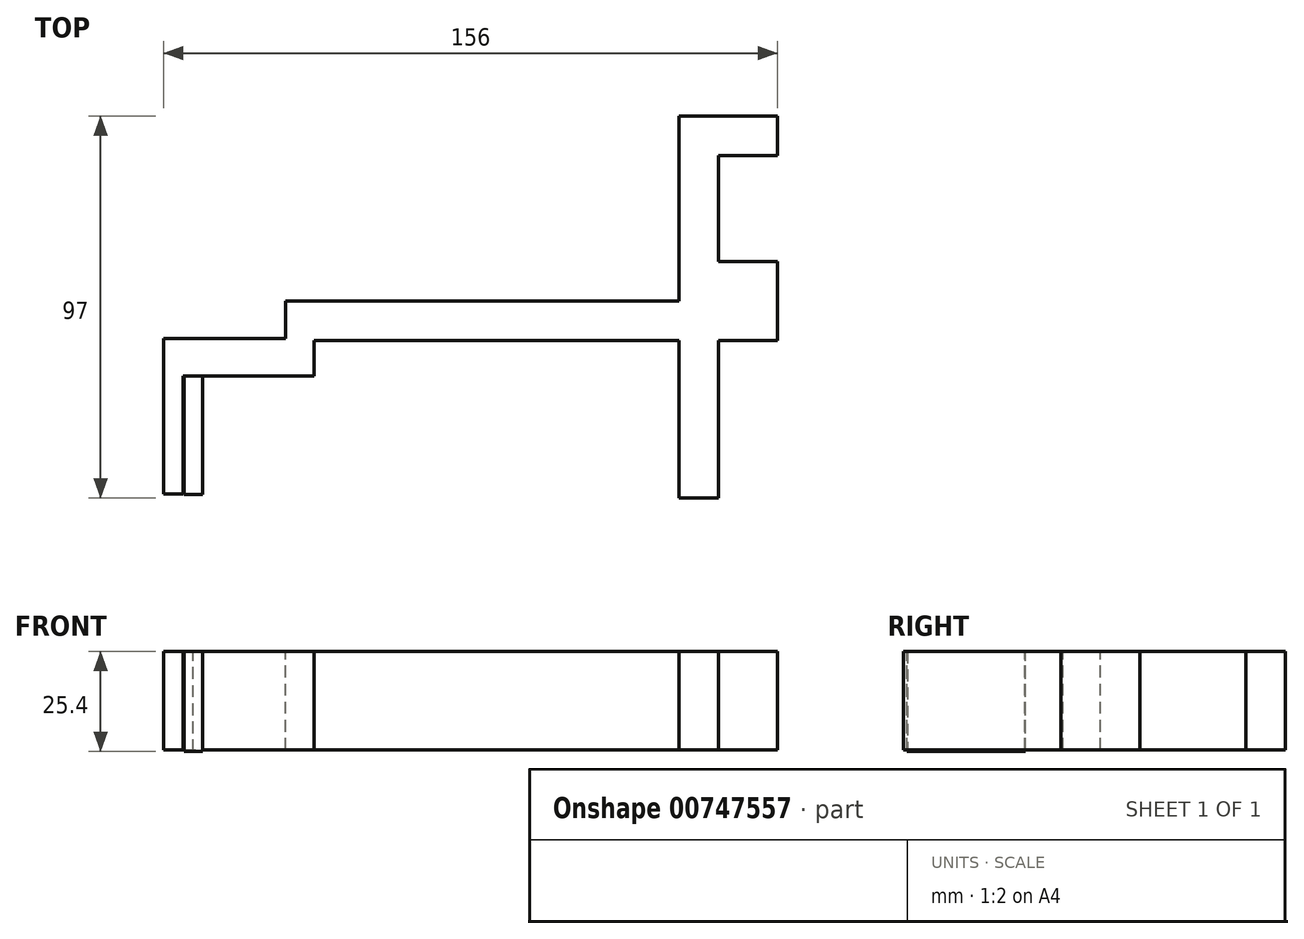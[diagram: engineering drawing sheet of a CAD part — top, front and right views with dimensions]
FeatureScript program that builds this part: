
annotation { "Feature Type Name" : "Feature", "Feature Type Description" : "" }
export const myFeature = defineFeature(function(context is Context, id is Id, definition is map)
    precondition{}
    {
        {
            var Q0;
            Q0=qCreatedBy(makeId("Front.planeOp"),FACE);
            var sketch = newSketch(context, id + "F0", { "sketchPlane" : qUnion([Q0])});
            skLineSegment(sketch, "E0.bottom", {"start": v(-55.45, 37.09) * mm, "end": v(59.55, 37.09) * mm});
            skLineSegment(sketch, "E0.top", {"start": v(-55.45, 12.09) * mm, "end": v(59.55, 12.09) * mm});
            skLineSegment(sketch, "E0.left", {"start": v(-55.45, 37.09) * mm, "end": v(-55.45, 12.09) * mm});
            skLineSegment(sketch, "E0.right", {"start": v(59.55, 37.09) * mm, "end": v(59.55, 12.09) * mm});
            skSolve(sketch);
        }
        {
            var Q0;
            Q0=makeQuery(id+"F0.imprint","IMPRINT",FACE,{"disambiguationData":[TD([[makeQuery(id+"F0.imprint","IMPRINT",EDGE,{"derivedFrom":sQuery(id+"F0.wireOp",EDGE,"E0.bottom")}),-1.0]])]});
            extrude(context, id + "F1", {"entities" : qUnion([Q0]), "depth" : 10 * mm, "offsetDistance" : 25.4 * mm});
        }
        {
            var Q0;
            Q0=makeQuery(id+"F1.opExtrude","CAP_FACE",FACE,{"disambiguationData":[OSD([sQuery(id+"F0.wireOp",EDGE,"E0.bottom"),sQuery(id+"F0.wireOp",EDGE,"E0.top"),sQuery(id+"F0.wireOp",EDGE,"E0.left"),sQuery(id+"F0.wireOp",EDGE,"E0.right")])],"isStart":false});
            var sketch = newSketch(context, id + "F2", { "sketchPlane" : qUnion([Q0])});
            skLineSegment(sketch, "E1", {"start": v(-55.45, 37.09) * mm, "end": v(-45.45, 37.09) * mm});
            skLineSegment(sketch, "E2", {"start": v(-45.45, 37.09) * mm, "end": v(-45.45, 12.09) * mm});
            skLineSegment(sketch, "E3", {"start": v(-45.45, 12.09) * mm, "end": v(-55.45, 12.09) * mm});
            skLineSegment(sketch, "E4", {"start": v(-55.45, 12.09) * mm, "end": v(-55.45, 37.09) * mm});
            skSolve(sketch);
        }
        {
            var Q0;
            Q0=makeQuery(id+"F2.imprint","IMPRINT",FACE,{"disambiguationData":[TD([[makeQuery(id+"F2.imprint","IMPRINT",EDGE,{"derivedFrom":sQuery(id+"F2.wireOp",EDGE,"E1")}),-1.0]])]});
            extrude(context, id + "F3", {"entities" : qUnion([Q0]), "operationType" : NewBodyOperationType.ADD, "depth" : 9.05 * mm, "offsetDistance" : 25.4 * mm});
        }
        {
            var Q0;
            Q0=makeQuery(id+"F1.opExtrude","CAP_FACE",FACE,{"disambiguationData":[OSD([sQuery(id+"F0.wireOp",EDGE,"E0.bottom"),sQuery(id+"F0.wireOp",EDGE,"E0.top"),sQuery(id+"F0.wireOp",EDGE,"E0.left"),sQuery(id+"F0.wireOp",EDGE,"E0.right")])],"isStart":false});
            var sketch = newSketch(context, id + "F4", { "sketchPlane" : qUnion([Q0])});
            skLineSegment(sketch, "E5", {"start": v(59.55, 8.34) * mm, "end": v(54.55, 8.34) * mm});
            skLineSegment(sketch, "E6", {"start": v(54.55, 12.09) * mm, "end": v(44.55, 12.09) * mm});
            skLineSegment(sketch, "E7", {"start": v(54.55, 12.09) * mm, "end": v(54.55, 37.09) * mm});
            skLineSegment(sketch, "E8", {"start": v(44.55, 12.09) * mm, "end": v(44.55, 37.09) * mm});
            skLineSegment(sketch, "E9", {"start": v(44.55, 37.09) * mm, "end": v(54.55, 37.09) * mm});
            skSolve(sketch);
        }
        {
            var Q0;
            Q0=makeQuery(id+"F4.imprint","IMPRINT",FACE,{"disambiguationData":[TD([[makeQuery(id+"F4.imprint","IMPRINT",EDGE,{"derivedFrom":sQuery(id+"F4.wireOp",EDGE,"E6")}),1.0]])]});
            extrude(context, id + "F5", {"entities" : qUnion([Q0]), "operationType" : NewBodyOperationType.ADD, "depth" : 40 * mm, "offsetDistance" : 25.4 * mm});
        }
        {
            var Q0;
            Q0=makeQuery(id+"F1.opExtrude","CAP_FACE",FACE,{"disambiguationData":[OSD([sQuery(id+"F0.wireOp",EDGE,"E0.bottom"),sQuery(id+"F0.wireOp",EDGE,"E0.top"),sQuery(id+"F0.wireOp",EDGE,"E0.left"),sQuery(id+"F0.wireOp",EDGE,"E0.right")])],"isStart":true});
            var sketch = newSketch(context, id + "F6", { "sketchPlane" : qUnion([Q0])});
            skLineSegment(sketch, "E10", {"start": v(-59.55, -12.94) * mm, "end": v(-44.55, -12.94) * mm});
            skLineSegment(sketch, "E11", {"start": v(-59.55, 12.09) * mm, "end": v(-44.55, 12.09) * mm});
            skLineSegment(sketch, "E12", {"start": v(-44.55, 12.09) * mm, "end": v(-44.55, 37.09) * mm});
            skLineSegment(sketch, "E13", {"start": v(-44.55, 37.09) * mm, "end": v(-59.55, 37.09) * mm});
            skLineSegment(sketch, "E14", {"start": v(-59.55, 37.09) * mm, "end": v(-59.55, 12.09) * mm});
            skSolve(sketch);
        }
        {
            var Q0;
            Q0=makeQuery(id+"F6.imprint","IMPRINT",FACE,{"disambiguationData":[TD([[makeQuery(id+"F6.imprint","IMPRINT",EDGE,{"derivedFrom":sQuery(id+"F6.wireOp",EDGE,"E11")}),-1.0]])]});
            extrude(context, id + "F7", {"entities" : qUnion([Q0]), "operationType" : NewBodyOperationType.ADD, "depth" : 47 * mm, "offsetDistance" : 25.4 * mm});
        }
        {
            var Q0;
            Q0=makeQuery(id+"F7.boolean.opBoolean","MERGE",FACE,{"derivedFrom":[makeQuery(id+"F5.boolean.opBoolean","MERGE",FACE,{"derivedFrom":[makeQuery(id+"F3.boolean.opBoolean","MERGE",FACE,{"derivedFrom":[makeQuery(id+"F1.opExtrude","SWEPT_FACE",FACE,{"disambiguationData":[OSD([sQuery(id+"F0.wireOp",EDGE,"E0.top")])]}),makeQuery(id+"F3.opExtrude","SWEPT_FACE",FACE,{"disambiguationData":[OSD([sQuery(id+"F2.wireOp",EDGE,"E3")])]})]}),makeQuery(id+"F5.opExtrude","SWEPT_FACE",FACE,{"disambiguationData":[OSD([sQuery(id+"F4.wireOp",EDGE,"E6")])]})]}),makeQuery(id+"F7.opExtrude","SWEPT_FACE",FACE,{"disambiguationData":[OSD([sQuery(id+"F6.wireOp",EDGE,"E11")])]})]});
            var sketch = newSketch(context, id + "F8", { "sketchPlane" : qUnion([Q0])});
            skLineSegment(sketch, "E15", {"start": v(51.76, 0) * mm, "end": v(51.76, -10) * mm});
            skLineSegment(sketch, "E16", {"start": v(59.55, -68.62) * mm, "end": v(54.55, -68.62) * mm});
            skLineSegment(sketch, "E17", {"start": v(59.55, -10) * mm, "end": v(59.55, -37) * mm});
            skLineSegment(sketch, "E18", {"start": v(54.55, -10) * mm, "end": v(59.55, -10) * mm});
            skLineSegment(sketch, "E19", {"start": v(54.55, -37) * mm, "end": v(59.55, -37) * mm});
            skLineSegment(sketch, "E20", {"start": v(54.55, -10) * mm, "end": v(54.55, -37) * mm});
            skSolve(sketch);
        }
        {
            var Q0;
            Q0=makeQuery(id+"F8.imprint","IMPRINT",FACE,{"disambiguationData":[TD([[makeQuery(id+"F8.imprint","IMPRINT",EDGE,{"derivedFrom":sQuery(id+"F8.wireOp",EDGE,"E17")}),-1.0]])]});
            extrude(context, id + "F9", {"entities" : qUnion([Q0]), "operationType" : NewBodyOperationType.REMOVE, "oppositeDirection" : true, "depth" : 25 * mm, "offsetDistance" : 25.4 * mm});
        }
        {
            var Q0;
            Q0=makeQuery(id+"F3.boolean.opBoolean","MERGE",FACE,{"derivedFrom":[makeQuery(id+"F1.opExtrude","SWEPT_FACE",FACE,{"disambiguationData":[OSD([sQuery(id+"F0.wireOp",EDGE,"E0.left")])]}),makeQuery(id+"F3.opExtrude","SWEPT_FACE",FACE,{"disambiguationData":[OSD([sQuery(id+"F2.wireOp",EDGE,"E4")])]})]});
            var sketch = newSketch(context, id + "F10", { "sketchPlane" : qUnion([Q0])});
            skLineSegment(sketch, "E21", {"start": v(19.05, 12.09) * mm, "end": v(9.53, 12.09) * mm});
            skLineSegment(sketch, "E22", {"start": v(9.53, 12.09) * mm, "end": v(9.53, 37.09) * mm});
            skLineSegment(sketch, "E23", {"start": v(9.53, 37.09) * mm, "end": v(19.05, 37.09) * mm});
            skSolve(sketch);
        }
        {
            var Q0;
            Q0=makeQuery(id+"F10.imprint","IMPRINT",FACE,{"disambiguationData":[TD([[makeQuery(id+"F10.imprint","IMPRINT",EDGE,{"derivedFrom":sQuery(id+"F10.wireOp",EDGE,"E21")}),-1.0]])]});
            extrude(context, id + "F11", {"entities" : qUnion([Q0]), "operationType" : NewBodyOperationType.ADD, "depth" : 36 * mm, "offsetDistance" : 25.4 * mm});
        }
        {
            var Q0;
            {var subQ0=sQuery(id+"F2.wireOp",EDGE,"E4");Q0=makeQuery(id+"F11.boolean.opBoolean","MERGE",FACE,{"derivedFrom":[makeQuery(id+"F3.opExtrude","CAP_FACE",FACE,{"disambiguationData":[OSD([sQuery(id+"F2.wireOp",EDGE,"E1"),sQuery(id+"F2.wireOp",EDGE,"E2"),sQuery(id+"F2.wireOp",EDGE,"E3"),subQ0])],"isStart":false}),makeQuery(id+"F11.opExtrude","SWEPT_FACE",FACE,{"disambiguationData":[OSD([subQ0])]})]});}
            var sketch = newSketch(context, id + "F12", { "sketchPlane" : qUnion([Q0])});
            skLineSegment(sketch, "E24", {"start": v(-91.45, 37.09) * mm, "end": v(-81.45, 37.09) * mm});
            skLineSegment(sketch, "E25", {"start": v(-81.45, 37.09) * mm, "end": v(-81.45, 12.09) * mm});
            skLineSegment(sketch, "E26", {"start": v(-81.45, 12.09) * mm, "end": v(-91.45, 12.09) * mm});
            skLineSegment(sketch, "E27", {"start": v(-91.45, 12.09) * mm, "end": v(-91.45, 37.09) * mm});
            skSolve(sketch);
        }
        {
            var Q0;
            Q0=makeQuery(id+"F12.imprint","IMPRINT",FACE,{"disambiguationData":[TD([[makeQuery(id+"F12.imprint","IMPRINT",EDGE,{"derivedFrom":sQuery(id+"F12.wireOp",EDGE,"E24")}),-1.0]])]});
            extrude(context, id + "F13", {"entities" : qUnion([Q0]), "operationType" : NewBodyOperationType.ADD, "depth" : 30 * mm, "offsetDistance" : 25.4 * mm});
        }
        {
            var Q0;
            {var subQ1=sQuery(id+"F0.wireOp",EDGE,"E0.right");Q0=makeQuery(id+"F9.boolean.opBoolean","SPLIT",FACE,{"disambiguationData":[TD([makeQuery(id+"F9.opExtrude","SWEPT_FACE",FACE,{"disambiguationData":[OSD([sQuery(id+"F8.wireOp",EDGE,"E18")])]})])],"derivedFrom":makeQuery(id+"F7.boolean.opBoolean","MERGE",FACE,{"derivedFrom":[makeQuery(id+"F1.opExtrude","SWEPT_FACE",FACE,{"disambiguationData":[OSD([subQ1])]}),makeQuery(id+"F7.opExtrude","SWEPT_FACE",FACE,{"disambiguationData":[OSD([sQuery(id+"F6.wireOp",EDGE,"E14")])]})]})});}
            extrude(context, id + "F14", {"entities" : qUnion([Q0]), "operationType" : NewBodyOperationType.ADD, "depth" : 10 * mm, "offsetDistance" : 25.4 * mm});
        }
        {
            var Q0;
            {var subQ1=sQuery(id+"F6.wireOp",EDGE,"E14");Q0=makeQuery(id+"F9.boolean.opBoolean","SPLIT",FACE,{"disambiguationData":[TD([makeQuery(id+"F9.opExtrude","SWEPT_FACE",FACE,{"disambiguationData":[OSD([sQuery(id+"F8.wireOp",EDGE,"E19")])]})])],"derivedFrom":makeQuery(id+"F7.boolean.opBoolean","MERGE",FACE,{"derivedFrom":[makeQuery(id+"F1.opExtrude","SWEPT_FACE",FACE,{"disambiguationData":[OSD([sQuery(id+"F0.wireOp",EDGE,"E0.right")])]}),makeQuery(id+"F7.opExtrude","SWEPT_FACE",FACE,{"disambiguationData":[OSD([subQ1])]})]})});}
            extrude(context, id + "F15", {"entities" : qUnion([Q0]), "operationType" : NewBodyOperationType.ADD, "depth" : 10 * mm, "offsetDistance" : 25.4 * mm});
        }
        {
            var Q0;
            {var subQ0=sQuery(id+"F6.wireOp",EDGE,"E14");var subQ1=sQuery(id+"F6.wireOp",EDGE,"E13");var subQ2=sQuery(id+"F0.wireOp",EDGE,"E0.right");var subQ3=sQuery(id+"F0.wireOp",EDGE,"E0.bottom");Q0=makeQuery(id+"F15.boolean.opBoolean","MERGE",FACE,{"derivedFrom":[makeQuery(id+"F14.boolean.opBoolean","MERGE",FACE,{"derivedFrom":[makeQuery(id+"F13.boolean.opBoolean","MERGE",FACE,{"derivedFrom":[makeQuery(id+"F11.boolean.opBoolean","MERGE",FACE,{"derivedFrom":[makeQuery(id+"F7.boolean.opBoolean","MERGE",FACE,{"derivedFrom":[makeQuery(id+"F5.boolean.opBoolean","MERGE",FACE,{"derivedFrom":[makeQuery(id+"F3.boolean.opBoolean","MERGE",FACE,{"derivedFrom":[makeQuery(id+"F1.opExtrude","SWEPT_FACE",FACE,{"disambiguationData":[OSD([subQ3])]}),makeQuery(id+"F3.opExtrude","SWEPT_FACE",FACE,{"disambiguationData":[OSD([sQuery(id+"F2.wireOp",EDGE,"E1")])]})]}),makeQuery(id+"F5.opExtrude","SWEPT_FACE",FACE,{"disambiguationData":[OSD([sQuery(id+"F4.wireOp",EDGE,"E9")])]})]}),makeQuery(id+"F7.opExtrude","SWEPT_FACE",FACE,{"disambiguationData":[OSD([subQ1])]})]}),makeQuery(id+"F11.opExtrude","SWEPT_FACE",FACE,{"disambiguationData":[OSD([sQuery(id+"F10.wireOp",EDGE,"E23")])]})]}),makeQuery(id+"F13.opExtrude","SWEPT_FACE",FACE,{"disambiguationData":[OSD([sQuery(id+"F12.wireOp",EDGE,"E24")])]})]}),makeQuery(id+"F14.opExtrude","SWEPT_FACE",FACE,{"disambiguationData":[OSD([subQ3,subQ2,subQ1,subQ0])]})]}),makeQuery(id+"F15.opExtrude","SWEPT_FACE",FACE,{"disambiguationData":[OSD([subQ3,subQ2,subQ1,subQ0])]})]});}
            var sketch = newSketch(context, id + "F16", { "sketchPlane" : qUnion([Q0])});
            skLineSegment(sketch, "E28", {"start": v(-45.45, -10) * mm, "end": v(-48.23, -10) * mm});
            skLineSegment(sketch, "E29", {"start": v(-48.23, -10) * mm, "end": v(-48.23, -19.05) * mm});
            skLineSegment(sketch, "E30", {"start": v(-48.23, -19.05) * mm, "end": v(-45.45, -19.05) * mm});
            skLineSegment(sketch, "E31", {"start": v(-45.45, -19.05) * mm, "end": v(-45.45, -10) * mm});
            skSolve(sketch);
        }
        {
            var Q0;
            Q0=makeQuery(id+"F16.imprint","IMPRINT",FACE,{"disambiguationData":[TD([[makeQuery(id+"F16.imprint","IMPRINT",EDGE,{"derivedFrom":sQuery(id+"F16.wireOp",EDGE,"E28")}),1.0]])]});
            extrude(context, id + "F17", {"entities" : qUnion([Q0]), "operationType" : NewBodyOperationType.REMOVE, "oppositeDirection" : true, "depth" : 25 * mm, "offsetDistance" : 25.4 * mm});
        }
        {
            var Q0;
            {var subQ0=sQuery(id+"F6.wireOp",EDGE,"E14");var subQ1=sQuery(id+"F6.wireOp",EDGE,"E13");var subQ2=sQuery(id+"F0.wireOp",EDGE,"E0.right");var subQ3=sQuery(id+"F0.wireOp",EDGE,"E0.bottom");Q0=makeQuery(id+"F15.boolean.opBoolean","MERGE",FACE,{"derivedFrom":[makeQuery(id+"F14.boolean.opBoolean","MERGE",FACE,{"derivedFrom":[makeQuery(id+"F13.boolean.opBoolean","MERGE",FACE,{"derivedFrom":[makeQuery(id+"F11.boolean.opBoolean","MERGE",FACE,{"derivedFrom":[makeQuery(id+"F7.boolean.opBoolean","MERGE",FACE,{"derivedFrom":[makeQuery(id+"F5.boolean.opBoolean","MERGE",FACE,{"derivedFrom":[makeQuery(id+"F3.boolean.opBoolean","MERGE",FACE,{"derivedFrom":[makeQuery(id+"F1.opExtrude","SWEPT_FACE",FACE,{"disambiguationData":[OSD([subQ3])]}),makeQuery(id+"F3.opExtrude","SWEPT_FACE",FACE,{"disambiguationData":[OSD([sQuery(id+"F2.wireOp",EDGE,"E1")])]})]}),makeQuery(id+"F5.opExtrude","SWEPT_FACE",FACE,{"disambiguationData":[OSD([sQuery(id+"F4.wireOp",EDGE,"E9")])]})]}),makeQuery(id+"F7.opExtrude","SWEPT_FACE",FACE,{"disambiguationData":[OSD([subQ1])]})]}),makeQuery(id+"F11.opExtrude","SWEPT_FACE",FACE,{"disambiguationData":[OSD([sQuery(id+"F10.wireOp",EDGE,"E23")])]})]}),makeQuery(id+"F13.opExtrude","SWEPT_FACE",FACE,{"disambiguationData":[OSD([sQuery(id+"F12.wireOp",EDGE,"E24")])]})]}),makeQuery(id+"F14.opExtrude","SWEPT_FACE",FACE,{"disambiguationData":[OSD([subQ3,subQ2,subQ1,subQ0])]})]}),makeQuery(id+"F15.opExtrude","SWEPT_FACE",FACE,{"disambiguationData":[OSD([subQ3,subQ2,subQ1,subQ0])]})]});}
            var sketch = newSketch(context, id + "F18", { "sketchPlane" : qUnion([Q0])});
            skLineSegment(sketch, "E32", {"start": v(-81.45, -19.05) * mm, "end": v(-76.45, -19.05) * mm});
            skLineSegment(sketch, "E33", {"start": v(-91.45, -9.53) * mm, "end": v(-86.45, -9.53) * mm});
            skLineSegment(sketch, "E34", {"start": v(-86.45, -9.53) * mm, "end": v(-86.45, -49.05) * mm});
            skLineSegment(sketch, "E35", {"start": v(-86.45, -49.05) * mm, "end": v(-91.45, -49.05) * mm});
            skLineSegment(sketch, "E36", {"start": v(-91.45, -49.05) * mm, "end": v(-91.45, -9.53) * mm});
            skSolve(sketch);
        }
        {
            var Q0;
            {var subQ10=sQuery(id+"F18.wireOp",EDGE,"E32");Q0=makeQuery(id+"F18.imprint","IMPRINT",FACE,{"disambiguationData":[TD([[makeQuery(id+"F18.imprint","IMPRINT",EDGE,{"derivedFrom":subQ10}),1.0]])]});}
            var sketch = newSketch(context, id + "F19", { "sketchPlane" : qUnion([Q0])});
            skLineSegment(sketch, "E37", {"start": v(-76.5, -19.14) * mm, "end": v(-76.5, -49.09) * mm});
            skLineSegment(sketch, "E38", {"start": v(-76.5, -49.09) * mm, "end": v(-81.3, -49.09) * mm});
            skLineSegment(sketch, "E39", {"start": v(-81.3, -49.09) * mm, "end": v(-81.3, -18.97) * mm});
            skLineSegment(sketch, "E40", {"start": v(-81.3, -18.97) * mm, "end": v(-76.5, -19.14) * mm});
            skSolve(sketch);
        }
        {
            var Q0;
            Q0=makeQuery(id+"F18.imprint","IMPRINT",FACE,{"disambiguationData":[TD([[makeQuery(id+"F18.imprint","IMPRINT",EDGE,{"derivedFrom":sQuery(id+"F18.wireOp",EDGE,"E33")}),-1.0]])]});
            extrude(context, id + "F20", {"entities" : qUnion([Q0]), "operationType" : NewBodyOperationType.REMOVE, "oppositeDirection" : true, "depth" : 25 * mm, "offsetDistance" : 25.4 * mm});
        }
        {
            var Q0;
            {var subQ5=sQuery(id+"F19.wireOp",EDGE,"E37");Q0=makeQuery(id+"F19.imprint","IMPRINT",FACE,{"disambiguationData":[TD([[makeQuery(id+"F19.imprint","IMPRINT",EDGE,{"derivedFrom":subQ5}),-1.0]])]});}
            extrude(context, id + "F21", {"entities" : qUnion([Q0]), "oppositeDirection" : true, "depth" : 25.4 * mm, "offsetDistance" : 25.4 * mm});
        }
    });
